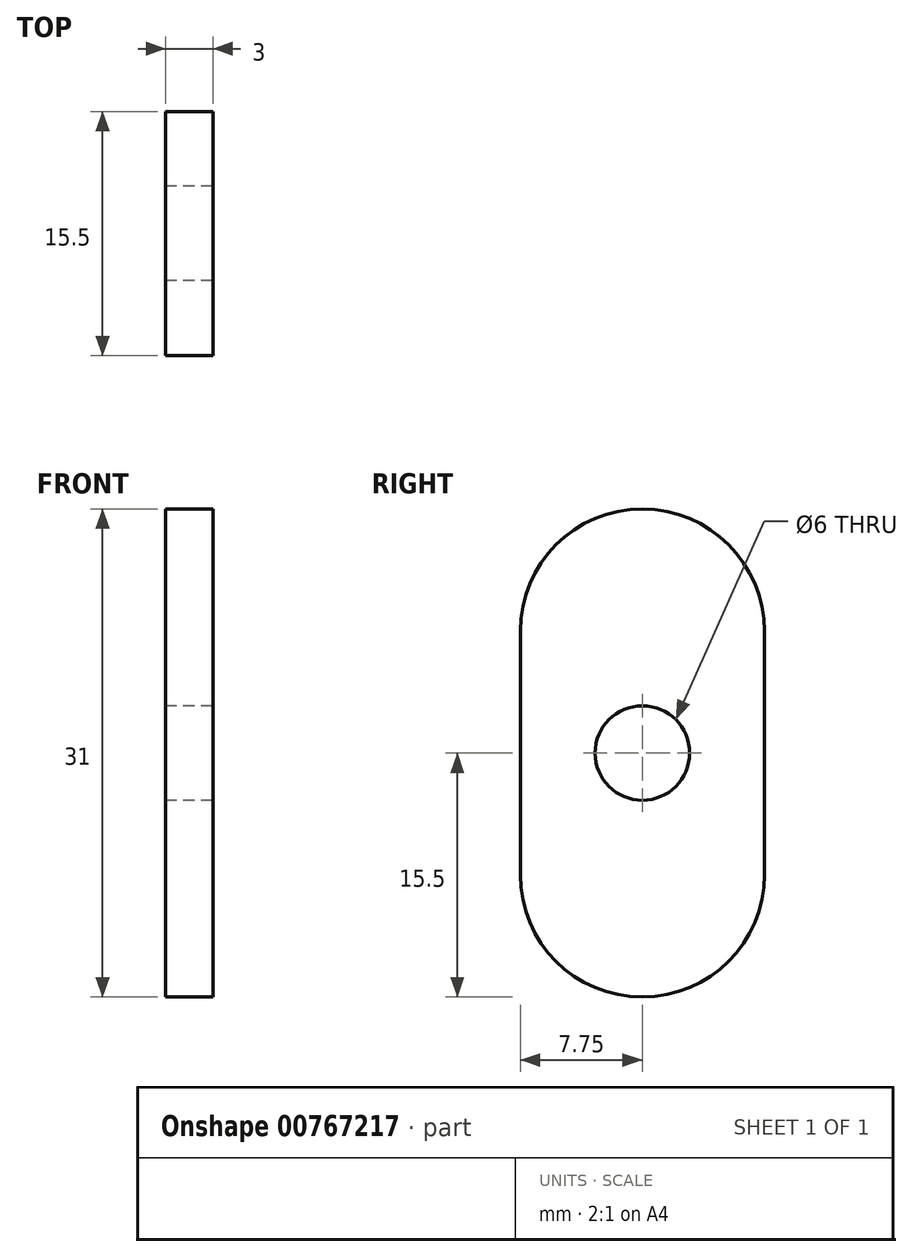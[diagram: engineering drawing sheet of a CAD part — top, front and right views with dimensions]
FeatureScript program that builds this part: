
annotation { "Feature Type Name" : "Feature", "Feature Type Description" : "" }
export const myFeature = defineFeature(function(context is Context, id is Id, definition is map)
    precondition{}
    {
        {
            var Q0;
            Q0=qCreatedBy(makeId("Right.planeOp"),FACE);
            var sketch = newSketch(context, id + "F0", { "sketchPlane" : qUnion([Q0])});
            skArc(sketch, "E0", {"start": v(-7.75, 7.75) * mm, "mid": v(0, 15.5) * mm, "end": v(7.75, 7.75) * mm});
            skLineSegment(sketch, "E1", {"start": v(-7.75, 7.75) * mm, "end": v(-7.75, 0) * mm});
            skLineSegment(sketch, "E2", {"start": v(7.75, 7.75) * mm, "end": v(7.75, 0) * mm});
            skLineSegment(sketch, "E3.MirrorCS", {"start": v(-7.75, -7.75) * mm, "end": v(-7.75, 0) * mm});
            skLineSegment(sketch, "E4.MirrorCS", {"start": v(7.75, -7.75) * mm, "end": v(7.75, 0) * mm});
            skArc(sketch, "E5.MirrorCS", {"start": v(-7.75, -7.75) * mm, "mid": v(0, -15.5) * mm, "end": v(7.75, -7.75) * mm});
            skCircle(sketch, "E6", {"center": v(0, 0) * mm, "radius": 3 * mm});
            skSolve(sketch);
        }
        {
            var Q0;
            Q0 = qSketchRegion(id + "F0", true);
            extrude(context, id + "F1", {"entities" : qUnion([Q0]), "endBound" : BoundingType.SYMMETRIC, "depth" : 3 * mm, "offsetDistance" : 25 * mm});
        }
    });
